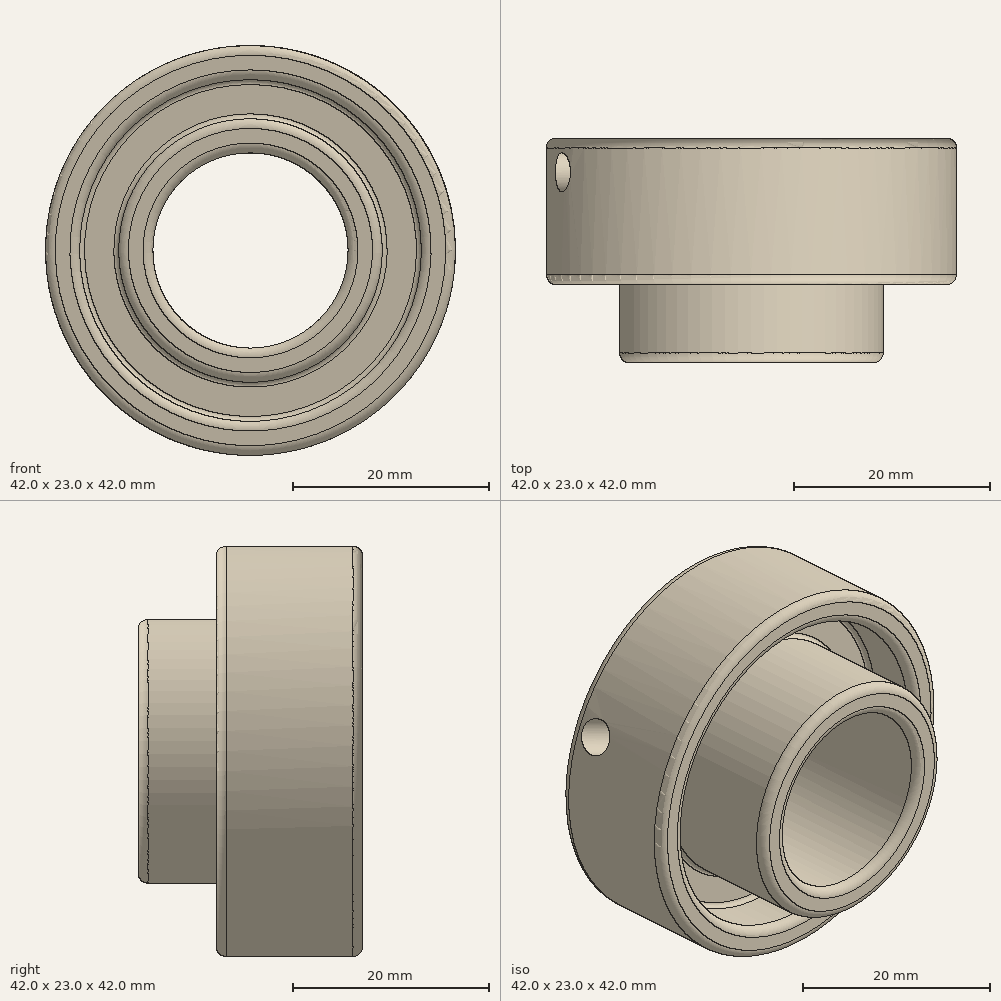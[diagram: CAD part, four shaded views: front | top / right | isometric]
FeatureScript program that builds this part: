
annotation { "Feature Type Name" : "Feature", "Feature Type Description" : "" }
export const myFeature = defineFeature(function(context is Context, id is Id, definition is map)
    precondition{}
    {
        {
            var Q0;
            Q0=qCreatedBy(makeId("Right.planeOp"),FACE);
            var sketch = newSketch(context, id + "F0", { "sketchPlane" : qUnion([Q0])});
            skLineSegment(sketch, "E0", {"start": v(0, 10) * mm, "end": v(23, 10) * mm});
            skLineSegment(sketch, "E1", {"start": v(23, 10) * mm, "end": v(23, 21) * mm});
            skLineSegment(sketch, "E2", {"start": v(23, 21) * mm, "end": v(8, 21) * mm});
            skLineSegment(sketch, "E3", {"start": v(8, 21) * mm, "end": v(8, 17.5) * mm});
            skLineSegment(sketch, "E4", {"start": v(8, 17.5) * mm, "end": v(14.5, 17.5) * mm});
            skLineSegment(sketch, "E5", {"start": v(14.5, 17.5) * mm, "end": v(14.5, 13.5) * mm});
            skLineSegment(sketch, "E6", {"start": v(14.5, 13.5) * mm, "end": v(0, 13.5) * mm});
            skLineSegment(sketch, "E7", {"start": v(0, 13.5) * mm, "end": v(0, 10) * mm});
            skLineSegment(sketch, "E8", {"start": v(0, 0) * mm, "end": v(8.91, 0) * mm});
            skSolve(sketch);
        }
        {
            var Q0;
            Q0=makeQuery(id+"F0.imprint","IMPRINT",FACE,{"disambiguationData":[TD([[makeQuery(id+"F0.imprint","IMPRINT",EDGE,{"derivedFrom":sQuery(id+"F0.wireOp",EDGE,"E0")}),1.0]])]});
            var Q1;
            Q1=sQuery(id+"F0.wireOp",EDGE,"E8");
            revolve(context, id + "F1", {"entities" : qUnion([Q0]), "axis" : qUnion([Q1]), "revolveType" : RevolveType.FULL});
        }
        {
            var Q0;
            Q0=makeQuery(id+"F1.opRevolve","SWEPT_FACE",FACE,{"disambiguationData":[OSD([sQuery(id+"F0.wireOp",EDGE,"E1")])]});
            var sketch = newSketch(context, id + "F2", { "sketchPlane" : qUnion([Q0])});
            skCircle(sketch, "E9", {"center": v(0, 0) * mm, "radius": 18.5 * mm});
            skPoint(sketch, "E10", {"position": v(0, 18.5) * mm});
            skPoint(sketch, "E11", {"position": v(-18.5, 0) * mm});
            skPoint(sketch, "E12", {"position": v(18.5, 0) * mm});
            skPoint(sketch, "E13", {"position": v(0, -18.5) * mm});
            skSolve(sketch);
        }
        {
            var Q0;
            Q0=sQuery(id+"F2.wireOp",VERTEX,"E10");
            var Q1;
            Q1=sQuery(id+"F2.wireOp",VERTEX,"E12");
            var Q2;
            Q2=sQuery(id+"F2.wireOp",VERTEX,"E11");
            var Q3;
            Q3=sQuery(id+"F2.wireOp",VERTEX,"E13");
            var Q4;
            Q4=makeQuery(id+"F1.opRevolve","SWEPT_BODY",BODY,{"disambiguationData":[OSD([sQuery(id+"F0.wireOp",EDGE,"E0"),sQuery(id+"F0.wireOp",EDGE,"E1"),sQuery(id+"F0.wireOp",EDGE,"E2"),sQuery(id+"F0.wireOp",EDGE,"E3"),sQuery(id+"F0.wireOp",EDGE,"E4"),sQuery(id+"F0.wireOp",EDGE,"E5"),sQuery(id+"F0.wireOp",EDGE,"E6"),sQuery(id+"F0.wireOp",EDGE,"E7")])]});
            hole(context, id + "F3", {"style" : HoleStyle.SIMPLE, "endStyle" : HoleEndStyle.BLIND, "holeDiameter" : 3 * mm, "holeDepth" : 6 * mm, "startFromSketch" : true, "locations" : qUnion([Q0, Q1, Q2, Q3]), "scope" : qUnion([Q4])});
        }
        {
            var Q0;
            Q0=makeQuery(id+"F1.opRevolve","SWEPT_FACE",FACE,{"disambiguationData":[OSD([sQuery(id+"F0.wireOp",EDGE,"E1")])]});
            cPlane(context, id + "F4", {"entities" : qUnion([Q0]), "cplaneType" : CPlaneType.OFFSET, "offset" : 3.5 * mm, "oppositeDirection" : true, "width" : 150 * mm, "height" : 150 * mm});
        }
        {
            var Q0;
            Q0=qCreatedBy(id+"F4.planeOp",FACE);
            var sketch = newSketch(context, id + "F5", { "sketchPlane" : qUnion([Q0])});
            skCircle(sketch, "E14.0", {"center": v(0, 0) * mm, "radius": 21 * mm});
            skCircle(sketch, "E15.0", {"center": v(0, 0) * mm, "radius": 10 * mm});
            skLineSegment(sketch, "E16", {"start": v(0, 0) * mm, "end": v(19.4, 8.04) * mm});
            skSolve(sketch);
        }
        {
            var Q0;
            Q0=sQuery(id+"F5.wireOp",EDGE,"E16");
            var Q1;
            Q1=sQuery(id+"F5.wireOp",VERTEX,"E16.end");
            cPlane(context, id + "F6", {"entities" : qUnion([Q0, Q1]), "cplaneType" : CPlaneType.CURVE_POINT, "offset" : 25 * mm, "width" : 150 * mm, "height" : 150 * mm});
        }
        {
            var Q0;
            Q0=qCreatedBy(id+"F6.planeOp",FACE);
            var sketch = newSketch(context, id + "F7", { "sketchPlane" : qUnion([Q0])});
            skPoint(sketch, "E17", {"position": v(-302.1, -30.67) * mm});
            skPoint(sketch, "E18.0", {"position": v(-19.5, 0) * mm});
            skSolve(sketch);
        }
        {
            var Q0;
            Q0=sQuery(id+"F7.wireOp",VERTEX,"E18.0");
            var Q1;
            Q1=makeQuery(id+"F1.opRevolve","SWEPT_BODY",BODY,{"disambiguationData":[OSD([sQuery(id+"F0.wireOp",EDGE,"E0"),sQuery(id+"F0.wireOp",EDGE,"E1"),sQuery(id+"F0.wireOp",EDGE,"E2"),sQuery(id+"F0.wireOp",EDGE,"E3"),sQuery(id+"F0.wireOp",EDGE,"E4"),sQuery(id+"F0.wireOp",EDGE,"E5"),sQuery(id+"F0.wireOp",EDGE,"E6"),sQuery(id+"F0.wireOp",EDGE,"E7")])]});
            hole(context, id + "F8", {"style" : HoleStyle.SIMPLE, "endStyle" : HoleEndStyle.BLIND, "holeDiameter" : 4 * mm, "holeDepth" : 6 * mm, "startFromSketch" : true, "locations" : qUnion([Q0]), "scope" : qUnion([Q1])});
        }
        {
            var Q0;
            Q0=makeQuery(id+"F1.opRevolve","SWEPT_EDGE",EDGE,{"disambiguationData":[OSD([sQuery(id+"F0.wireOp",EDGE,"E6"),sQuery(id+"F0.wireOp",EDGE,"E7")])]});
            var Q1;
            Q1=makeQuery(id+"F1.opRevolve","SWEPT_EDGE",EDGE,{"disambiguationData":[OSD([sQuery(id+"F0.wireOp",EDGE,"E0"),sQuery(id+"F0.wireOp",EDGE,"E7")])]});
            var Q2;
            Q2=makeQuery(id+"F1.opRevolve","SWEPT_EDGE",EDGE,{"disambiguationData":[OSD([sQuery(id+"F0.wireOp",EDGE,"E3"),sQuery(id+"F0.wireOp",EDGE,"E4")])]});
            var Q3;
            Q3=makeQuery(id+"F1.opRevolve","SWEPT_EDGE",EDGE,{"disambiguationData":[OSD([sQuery(id+"F0.wireOp",EDGE,"E2"),sQuery(id+"F0.wireOp",EDGE,"E3")])]});
            fillet(context, id + "F9", {"entities" : qUnion([Q0, Q1, Q2, Q3]), "radius" : 1 * mm, "tangentPropagation" : true, "allowEdgeOverflow" : false});
        }
        {
            var Q0;
            Q0=makeQuery(id+"F1.opRevolve","SWEPT_EDGE",EDGE,{"disambiguationData":[OSD([sQuery(id+"F0.wireOp",EDGE,"E1"),sQuery(id+"F0.wireOp",EDGE,"E2")])]});
            fillet(context, id + "F10", {"entities" : qUnion([Q0]), "radius" : 1 * mm, "tangentPropagation" : true, "allowEdgeOverflow" : false});
        }
        {
            var Q0;
            Q0=makeQuery(id+"F1.opRevolve","SWEPT_FACE",FACE,{"disambiguationData":[OSD([sQuery(id+"F0.wireOp",EDGE,"E5")])]});
            fillet(context, id + "F11", {"entities" : qUnion([Q0]), "radius" : 0.5 * mm, "tangentPropagation" : true, "allowEdgeOverflow" : false});
        }
    });
